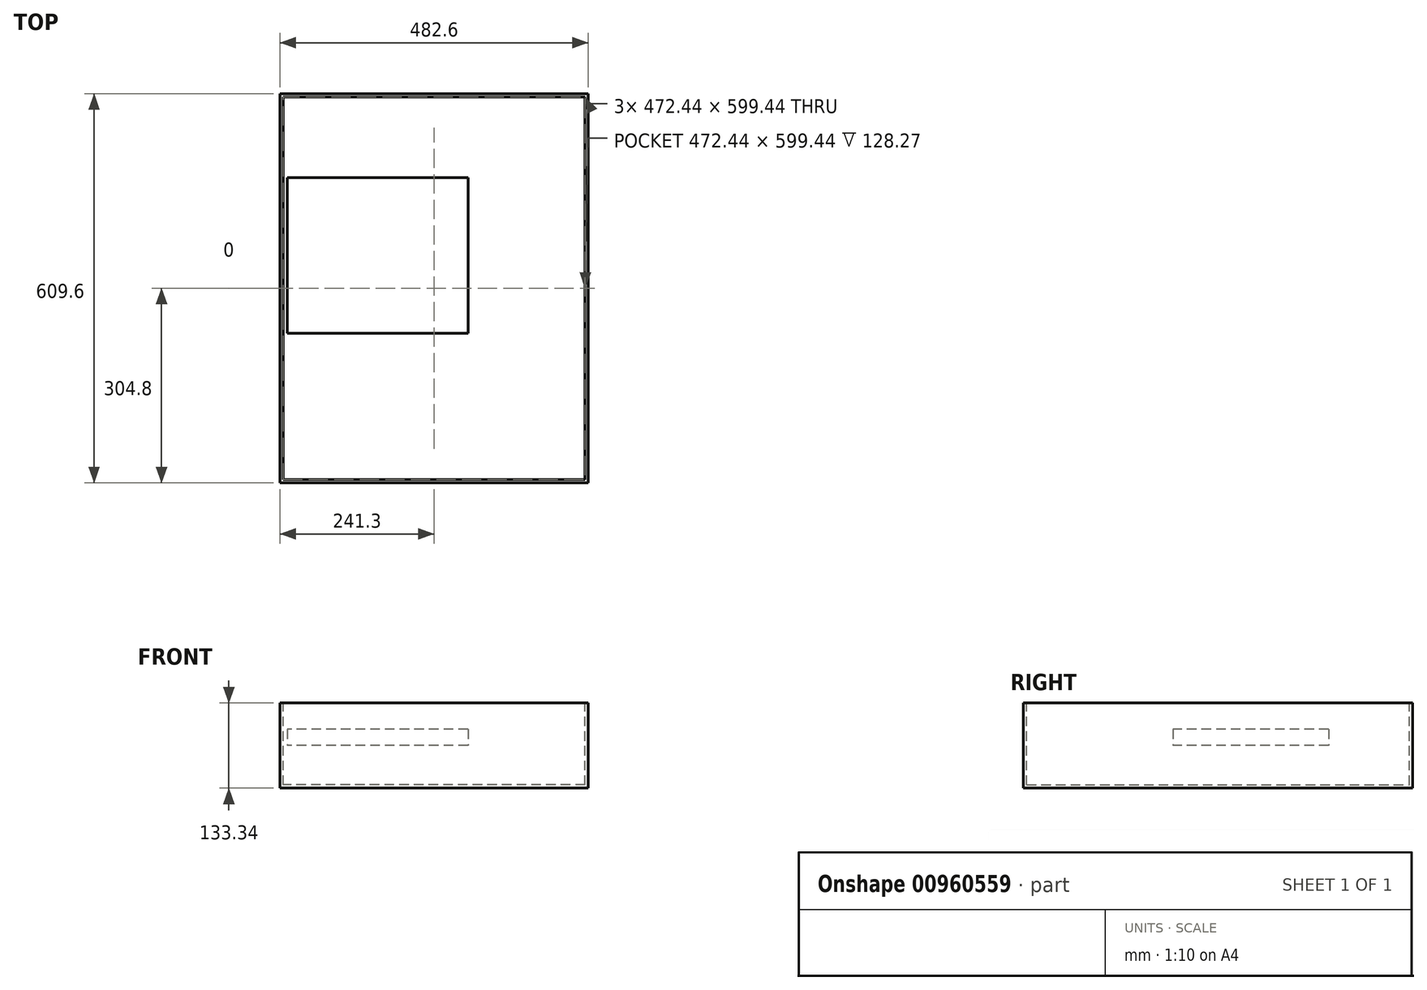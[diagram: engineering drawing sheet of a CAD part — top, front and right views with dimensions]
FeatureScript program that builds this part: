
annotation { "Feature Type Name" : "Feature", "Feature Type Description" : "" }
export const myFeature = defineFeature(function(context is Context, id is Id, definition is map)
    precondition{}
    {
        {
            var Q0;
            Q0=qCreatedBy(makeId("Front.planeOp"),FACE);
            var sketch = newSketch(context, id + "F0", { "sketchPlane" : qUnion([Q0])});
            skLineSegment(sketch, "E0.bottom", {"start": v(241.3, -66.67) * mm, "end": v(-241.3, -66.68) * mm});
            skLineSegment(sketch, "E0.top", {"start": v(241.3, 66.68) * mm, "end": v(-241.3, 66.67) * mm});
            skLineSegment(sketch, "E0.left", {"start": v(241.3, -66.67) * mm, "end": v(241.3, 66.68) * mm});
            skLineSegment(sketch, "E0.right", {"start": v(-241.3, -66.68) * mm, "end": v(-241.3, 66.67) * mm});
            skPoint(sketch, "E0.middle", {"position": v(0, 0) * mm});
            skSolve(sketch);
        }
        {
            var Q0;
            Q0=makeQuery(id+"F0.imprint","IMPRINT",FACE,{"disambiguationData":[TD([[makeQuery(id+"F0.imprint","IMPRINT",EDGE,{"derivedFrom":sQuery(id+"F0.wireOp",EDGE,"E0.bottom")}),-1.0]])]});
            var Q1;
            Q1=sQuery(id+"F0.wireOp",EDGE,"E0.right");
            var Q2;
            Q2=sQuery(id+"F0.wireOp",EDGE,"E0.bottom");
            var Q3;
            Q3=sQuery(id+"F0.wireOp",EDGE,"E0.left");
            var Q4;
            Q4=sQuery(id+"F0.wireOp",EDGE,"E0.top");
            extrude(context, id + "F1", {"entities" : qUnion([Q0]), "surfaceOperationType" : NewSurfaceOperationType.ADD, "surfaceEntities" : qUnion([Q1, Q2, Q3, Q4]), "depth" : 609.6 * mm, "offsetDistance" : 25.4 * mm});
        }
        {
            var Q0;
            Q0=qCreatedBy(makeId("Top.planeOp"),FACE);
            var sketch = newSketch(context, id + "F2", { "sketchPlane" : qUnion([Q0])});
            skLineSegment(sketch, "E1.bottom", {"start": v(52.93, -131.48) * mm, "end": v(-229.93, -131.48) * mm});
            skLineSegment(sketch, "E1.top", {"start": v(52.93, -375.32) * mm, "end": v(-229.93, -375.32) * mm});
            skLineSegment(sketch, "E1.left", {"start": v(52.93, -131.48) * mm, "end": v(52.93, -375.32) * mm});
            skPoint(sketch, "E1.middle", {"position": v(-99.47, -253.4) * mm});
            skLineSegment(sketch, "E2.0", {"start": v(-229.93, -131.48) * mm, "end": v(-229.93, -375.32) * mm});
            skPoint(sketch, "E1.right.end.orphan", {"position": v(-251.87, -375.32) * mm});
            skPoint(sketch, "E3.orphan", {"position": v(-251.87, -131.48) * mm});
            skSolve(sketch);
        }
        {
            var Q0;
            Q0=qSketchRegion(id+"F2",true);
            extrude(context, id + "F3", {"entities" : qUnion([Q0]), "depth" : 25.4 * mm, "offsetDistance" : 25.4 * mm});
        }
        {
            var Q0;
            Q0=makeQuery(id+"F1.opExtrude","SWEPT_FACE",FACE,{"disambiguationData":[OSD([sQuery(id+"F0.wireOp",EDGE,"E0.top")])]});
            shell(context, id + "F4", {"entities" : qUnion([Q0]), "thickness" : 5.08 * mm});
        }
    });
